FCSTD DOCUMENT  (FreeCAD 1.0R39109 (Git))
Label: lightModule
License: All rights reserved
LicenseURL: http://en.wikipedia.org/wiki/All_rights_reserved
objects: Part::Feature×41, Part::MultiFuse×37, Part::FeaturePython×27, Part::Extrusion×24, Sketcher::SketchObject×23, Part::Cylinder×20, Part::Cut×13, Part::Fillet×7, Part::Sphere×6, App::Part×5, Part::Compound×3, Part::Box×1, Part::Part2DObjectPython×1
note: 226 computed .brp shape members not serialized (recipe doc carries the construction recipe); baked Part::Feature solids carry a one-line shape summary decoded from their .brp

FEATURE [Part::Feature] Part__Feature330  label="elpCamera"
  Placement = pos=(0,-270,13) rot=(0,0,1;0rad)
  shape: bbox 38 x 38 x 25.12 mm, 164 faces (baked)
FEATURE [Part::Box] Box004  label="guva"
  AttacherType = Attacher::AttachEngine3D
  Height = 2
  Length = 19
  Placement = pos=(-9.5,-88,0) rot=(0,0,1;0rad)
  Width = 10
FEATURE [Part::Cylinder] Cylinder098
  Angle = 360
  AttacherType = Attacher::AttachEngine3D
  FirstAngle = 0
  Height = 10
  Placement = pos=(6.5,-83,0) rot=(0,0,1;0rad)
  Radius = 1.13
  SecondAngle = 0
FEATURE [Part::Cut] Cut018  label="guva001"
  Base = -> Box004
  Placement = pos=(80,-176.25,28) rot=(0,0,1;0rad)
  Tool = -> Cylinder098
FEATURE [Part::Feature] Part__Feature105  label="Printed Circuit Board"
  shape: bbox 25.4 x 17.78 x 1.6 mm, 42 faces (baked)
FEATURE [Part::Feature] Part__Feature106  label="EAHC2835WD6"
  shape: bbox 3.513 x 2.813 x 0.7485 mm, 108 faces, 4 solids (baked)
FEATURE [Part::Feature] Part__Feature107  label="AS7341 v2"
  Placement = pos=(0,-0.339822,1.6) rot=(0,0,1;0rad)
  shape: bbox 2 x 3.1 x 1.1 mm, 267 faces, 26 solids (baked)
FEATURE [Part::Feature] Part__Feature108  label="CAPC-0805-T0.95-BN v1"
  Placement = pos=(-5.01759,-3.15294,1.6) rot=(0,0,1;0rad)
  shape: bbox 2.1 x 1.35 x 0.95 mm, 42 faces (baked)
FEATURE [Part::Feature] Part__Feature109  label="CAPC-0805-T0.95-BN v002"
  Placement = pos=(-5.48627,2.66154,1.6) rot=(0,0,-1;1.5708rad)
  shape: bbox 1.35 x 2.1 x 0.95 mm, 42 faces (baked)
FEATURE [Part::Feature] Part__Feature110  label="CAPC-0805-T0.95-BN v003"
  Placement = pos=(-3.43627,2.66154,1.6) rot=(0,0,-1;1.5708rad)
  shape: bbox 1.35 x 2.1 x 0.95 mm, 42 faces (baked)
FEATURE [Part::Feature] Part__Feature111  label="CAPC-0603-T0.9-BN v1"
  Placement = pos=(-1.69987,-3.28475,1.6) rot=(0,0,1;0rad)
  shape: bbox 1.7 x 0.9 x 0.9 mm, 42 faces (baked)
FEATURE [Part::Feature] Part__Feature112  label="BODY_MF06A"
  Placement = pos=(0,0,0.762) rot=(0.57735,-0.57735,-0.57735;2.0944rad)
  shape: bbox 1.601 x 2.921 x 1.016 mm, 42 faces (baked)
FEATURE [Part::Feature] Part__Feature113  label="LEAD_MF06A"
  Placement = pos=(-0.9652,-0.9525,0.1016) rot=(0.57735,-0.57735,-0.57735;2.0944rad)
  shape: bbox 0.6223 x 0.3749 x 0.8636 mm, 14 faces (baked)
FEATURE [Part::Feature] Part__Feature114  label="LEAD_MF06A001"
  Placement = pos=(-0.9652,0,0.1016) rot=(0.57735,-0.57735,-0.57735;2.0944rad)
  shape: bbox 0.6223 x 0.3749 x 0.8636 mm, 14 faces (baked)
FEATURE [Part::Feature] Part__Feature115  label="LEAD_MF06A002"
  Placement = pos=(-0.9652,0.9525,0.1016) rot=(0.57735,-0.57735,-0.57735;2.0944rad)
  shape: bbox 0.6223 x 0.3749 x 0.8636 mm, 14 faces (baked)
FEATURE [Part::Feature] Part__Feature116  label="LEAD_MF06A003"
  Placement = pos=(0.9652,-0.9525,0.1016) rot=(0.57735,0.57735,0.57735;2.0944rad)
  shape: bbox 0.6223 x 0.3749 x 0.8636 mm, 14 faces (baked)
FEATURE [Part::Feature] Part__Feature117  label="LEAD_MF06A004"
  Placement = pos=(0.9652,0,0.1016) rot=(0.57735,0.57735,0.57735;2.0944rad)
  shape: bbox 0.6223 x 0.3749 x 0.8636 mm, 14 faces (baked)
FEATURE [Part::Feature] Part__Feature118  label="LEAD_MF06A005"
  Placement = pos=(0.9652,0.9525,0.1016) rot=(0.57735,0.57735,0.57735;2.0944rad)
  shape: bbox 0.6223 x 0.3749 x 0.8636 mm, 14 faces (baked)
FEATURE [Part::Feature] Part__Feature119  label="SOT363 v2"
  Placement = pos=(4.97054,-0.645171,1.675) rot=(0,0,1;3.14159rad)
  shape: bbox 2.1 x 2 x 1.1 mm, 94 faces, 7 solids (baked)
FEATURE [Part::Feature] Part__Feature120  label="LED 0603 single color v1"
  Placement = pos=(-9.18406,3.72778,1.60762) rot=(0,0,1;1.5708rad)
  shape: bbox 1.961 x 0.7932 x 0.7145 mm, 63 faces, 5 solids (baked)
FEATURE [Part::Feature] Part__Feature121  label="RESC-0603 v1"
  Placement = pos=(4.83432,-3.67461,1.6) rot=(0,0,1;0rad)
  shape: bbox 1.7 x 0.9 x 0.55 mm, 52 faces, 3 solids (baked)
FEATURE [Part::Feature] Part__Feature122  label="RESC-0603 v002"
  Placement = pos=(-7.14949,3.61248,1.6) rot=(0,0,-1;1.5708rad)
  shape: bbox 0.9 x 1.7 x 0.55 mm, 52 faces, 3 solids (baked)
FEATURE [Part::Feature] Part__Feature123  label="YC164_RESPACK v1"
  Placement = pos=(2.99591,1.52916,1.6) rot=(0,0,1;0rad)
  shape: bbox 3.2 x 1.6 x 0.61 mm, 172 faces (baked)
FEATURE [Part::Feature] Part__Feature124  label="qwicc v2"
  Placement = pos=(-10.8364,0.0607456,1.65) rot=(0,0,-1;1.5708rad)
  shape: bbox 4.95 x 6 x 2.96 mm, 229 faces, 7 solids (baked)
FEATURE [Part::Feature] Part__Feature125  label="qwicc v003"
  Placement = pos=(10.8256,0.00556102,1.65) rot=(0,0,1;1.5708rad)
  shape: bbox 4.95 x 6 x 2.96 mm, 229 faces, 7 solids (baked)
FEATURE [App::Part] sot_23_6_v2  label="sot-23-6 v2"
  Group = -> [Part__Feature112,Part__Feature113,Part__Feature114,Part__Feature115,Part__Feature116,Part__Feature117,Part__Feature118]
  Origin = -> Origin008
  Placement = pos=(-4.47945,-0.603742,1.69152) rot=(0,0,1;0rad)
FEATURE [App::Part] Adafruit_AS7341_STEMMA_QT_v2  label="ltr390"
  Group = -> [Part__Feature105,Part__Feature106,Part__Feature107,Part__Feature108,Part__Feature109,Part__Feature110,Part__Feature111,sot_23_6_v2,Part__Feature119,Part__Feature120,Part__Feature121,Part__Feature122,Part__Feature123,Part__Feature124,Part__Feature125]
  Origin = -> Origin009
  Placement = pos=(80,-274.25,28) rot=(0,0,1;0rad)
FEATURE [Part::FeaturePython] Clone  label="tSlotTop"  # WARN: FeaturePython — macro-defined, semantics opaque (R4)
  AttacherType = Attacher::AttachEngine3D
  Fuse = false
  Placement = pos=(0,0,-7) rot=(1,0,0;1.5708rad)
  Scale = (1,1,3)
FEATURE [Part::Sphere] Sphere011  label="Sphere_out005"
  Angle1 = -90
  Angle2 = 90
  Angle3 = 180
  AttacherType = Attacher::AttachEngine3D
  Placement = pos=(0,0,0) rot=(1,0,0;1.5708rad)
  Radius = 30
FEATURE [Part::Sphere] Sphere012  label="Sphere_in005"
  Angle1 = -90
  Angle2 = 90
  Angle3 = 180
  AttacherType = Attacher::AttachEngine3D
  Placement = pos=(0,0,0) rot=(1,0,0;1.5708rad)
  Radius = 28.7
FEATURE [Part::Cut] Cut065  label="Dome005"
  Base = -> Sphere011
  Tool = -> Sphere012
FEATURE [Part::Cylinder] Cylinder139
  Angle = 360
  AttacherType = Attacher::AttachEngine3D
  FirstAngle = 0
  Height = 2.6
  Radius = 40
  SecondAngle = 0
FEATURE [Part::Cylinder] Cylinder140  label="Cylinder_in005"
  Angle = 360
  AttacherType = Attacher::AttachEngine3D
  FirstAngle = 0
  Height = 2.6
  Radius = 30
  SecondAngle = 0
FEATURE [Part::Cut] Cut066  label="Base_flat005"
  Base = -> Cylinder139
  Tool = -> Cylinder140
FEATURE [Part::MultiFuse] Fusion  label="dome"
  Shapes = -> [Cut065,Cut066]
FEATURE [Sketcher::SketchObject] Sketch194
  ArcFitTolerance = 0
  FullyConstrained = true
  MakeInternals = false
  sketch-geometry (4):
    g0: Circle CenterX=0 CenterY=35 CenterZ=0 NormalX=0 NormalY=0 NormalZ=1 AngleXU=0 Radius=1.625
    g1: Circle CenterX=35 CenterY=0 CenterZ=0 NormalX=0 NormalY=0 NormalZ=1 AngleXU=0 Radius=1.625
    g2: Circle CenterX=-35 CenterY=0 CenterZ=0 NormalX=0 NormalY=0 NormalZ=1 AngleXU=0 Radius=1.625
    g3: Circle CenterX=0 CenterY=-35 CenterZ=0 NormalX=0 NormalY=0 NormalZ=1 AngleXU=0 Radius=1.625
  constraints (12):
    c: PointOnObject(g0,g-2)
    c: PointOnObject(g1,g-1)
    c: PointOnObject(g2,g-1)
    c: PointOnObject(g3,g-2)
    c: DistanceY(g3,g-1) = 35
    c: DistanceX(g-1,g1) = 35
    c: DistanceX(g2,g-1) = 35
    c: DistanceY(g-1,g0) = 35
    c: Equal(g1,g3)
    c: Equal(g1,g2)
    c: Equal(g1,g0)
    c: Diameter(g1) = 3.25
FEATURE [Part::Extrusion] Extrude091
  Base = -> Sketch194
  Dir = (0,0,1)
  DirMode = 2
  FaceMakerClass = Part::FaceMakerBullseye
  FaceMakerMode = 3
  LengthFwd = 10
  LengthRev = 0
  Solid = true
  Symmetric = false
FEATURE [Part::Cut] Cut067  label="dome001"
  Base = -> Fusion
  Placement = pos=(0,-270,30.5) rot=(0,0,1;0rad)
  Tool = -> Extrude091
FEATURE [Part::Cylinder] Cylinder141
  Angle = 360
  AttacherType = Attacher::AttachEngine3D
  FirstAngle = 0
  Height = 2.6
  Radius = 40
  SecondAngle = 0
FEATURE [Part::Cylinder] Cylinder142  label="Cylinder_in006"
  Angle = 360
  AttacherType = Attacher::AttachEngine3D
  FirstAngle = 0
  Height = 2.6
  Radius = 30
  SecondAngle = 0
FEATURE [Part::Cut] Cut069  label="Base_flat006"
  Base = -> Cylinder141
  Tool = -> Cylinder142
FEATURE [Sketcher::SketchObject] Sketch195
  ArcFitTolerance = 0
  FullyConstrained = true
  MakeInternals = false
  sketch-geometry (4):
    g0: Circle CenterX=0 CenterY=35 CenterZ=0 NormalX=0 NormalY=0 NormalZ=1 AngleXU=0 Radius=1.625
    g1: Circle CenterX=35 CenterY=0 CenterZ=0 NormalX=0 NormalY=0 NormalZ=1 AngleXU=0 Radius=1.625
    g2: Circle CenterX=-35 CenterY=0 CenterZ=0 NormalX=0 NormalY=0 NormalZ=1 AngleXU=0 Radius=1.625
    g3: Circle CenterX=0 CenterY=-35 CenterZ=0 NormalX=0 NormalY=0 NormalZ=1 AngleXU=0 Radius=1.625
  constraints (12):
    c: PointOnObject(g0,g-2)
    c: PointOnObject(g1,g-1)
    c: PointOnObject(g2,g-1)
    c: PointOnObject(g3,g-2)
    c: DistanceY(g3,g-1) = 35
    c: DistanceX(g-1,g1) = 35
    c: DistanceX(g2,g-1) = 35
    c: DistanceY(g-1,g0) = 35
    c: Equal(g1,g3)
    c: Equal(g1,g2)
    c: Equal(g1,g0)
    c: Diameter(g1) = 3.25
FEATURE [Part::Extrusion] Extrude092
  Base = -> Sketch195
  Dir = (0,0,1)
  DirMode = 2
  FaceMakerClass = Part::FaceMakerBullseye
  FaceMakerMode = 3
  LengthFwd = 10
  LengthRev = 0
  Solid = true
  Symmetric = false
FEATURE [Part::Sphere] Sphere013  label="Sphere_out006"
  Angle1 = -90
  Angle2 = 90
  Angle3 = 180
  AttacherType = Attacher::AttachEngine3D
  Placement = pos=(0,0,0) rot=(1,0,0;1.5708rad)
  Radius = 30
FEATURE [Part::Sphere] Sphere014  label="Sphere_in006"
  Angle1 = -90
  Angle2 = 90
  Angle3 = 180
  AttacherType = Attacher::AttachEngine3D
  Placement = pos=(0,0,0) rot=(1,0,0;1.5708rad)
  Radius = 28.7
FEATURE [Part::Cut] Cut068  label="Dome006"
  Base = -> Sphere013
  Tool = -> Sphere014
FEATURE [Part::MultiFuse] Fusion187  label="dome003"
  Shapes = -> [Cut068,Cut069]
FEATURE [Part::Cut] Cut070  label="dome002"
  Base = -> Fusion187
  Placement = pos=(-80,-270,30.5) rot=(0,0,1;0rad)
  Tool = -> Extrude092
FEATURE [Part::Cylinder] Cylinder143
  Angle = 360
  AttacherType = Attacher::AttachEngine3D
  FirstAngle = 0
  Height = 2.6
  Radius = 40
  SecondAngle = 0
FEATURE [Part::Cylinder] Cylinder144  label="Cylinder_in007"
  Angle = 360
  AttacherType = Attacher::AttachEngine3D
  FirstAngle = 0
  Height = 2.6
  Radius = 30
  SecondAngle = 0
FEATURE [Part::Cut] Cut072  label="Base_flat007"
  Base = -> Cylinder143
  Tool = -> Cylinder144
FEATURE [Sketcher::SketchObject] Sketch196
  ArcFitTolerance = 0
  FullyConstrained = true
  MakeInternals = false
  sketch-geometry (4):
    g0: Circle CenterX=0 CenterY=35 CenterZ=0 NormalX=0 NormalY=0 NormalZ=1 AngleXU=0 Radius=1.625
    g1: Circle CenterX=35 CenterY=0 CenterZ=0 NormalX=0 NormalY=0 NormalZ=1 AngleXU=0 Radius=1.625
    g2: Circle CenterX=-35 CenterY=0 CenterZ=0 NormalX=0 NormalY=0 NormalZ=1 AngleXU=0 Radius=1.625
    g3: Circle CenterX=0 CenterY=-35 CenterZ=0 NormalX=0 NormalY=0 NormalZ=1 AngleXU=0 Radius=1.625
  constraints (12):
    c: PointOnObject(g0,g-2)
    c: PointOnObject(g1,g-1)
    c: PointOnObject(g2,g-1)
    c: PointOnObject(g3,g-2)
    c: DistanceY(g3,g-1) = 35
    c: DistanceX(g-1,g1) = 35
    c: DistanceX(g2,g-1) = 35
    c: DistanceY(g-1,g0) = 35
    c: Equal(g1,g3)
    c: Equal(g1,g2)
    c: Equal(g1,g0)
    c: Diameter(g1) = 3.25
FEATURE [Part::Extrusion] Extrude093
  Base = -> Sketch196
  Dir = (0,0,1)
  DirMode = 2
  FaceMakerClass = Part::FaceMakerBullseye
  FaceMakerMode = 3
  LengthFwd = 10
  LengthRev = 0
  Solid = true
  Symmetric = false
FEATURE [Part::Sphere] Sphere015  label="Sphere_out007"
  Angle1 = -90
  Angle2 = 90
  Angle3 = 180
  AttacherType = Attacher::AttachEngine3D
  Placement = pos=(0,0,0) rot=(1,0,0;1.5708rad)
  Radius = 30
FEATURE [Part::Sphere] Sphere016  label="Sphere_in007"
  Angle1 = -90
  Angle2 = 90
  Angle3 = 180
  AttacherType = Attacher::AttachEngine3D
  Placement = pos=(0,0,0) rot=(1,0,0;1.5708rad)
  Radius = 28.7
FEATURE [Part::Cut] Cut071  label="Dome007"
  Base = -> Sphere015
  Tool = -> Sphere016
FEATURE [Part::MultiFuse] Fusion188  label="dome005"
  Shapes = -> [Cut071,Cut072]
FEATURE [Part::Cut] Cut073  label="dome004"
  Base = -> Fusion188
  Placement = pos=(80,-270,30.5) rot=(0,0,1;0rad)
  Tool = -> Extrude093
FEATURE [Sketcher::SketchObject] Sketch
  ArcFitTolerance = 0
  FullyConstrained = true
  MakeInternals = false
  Placement = pos=(0,0,27.5) rot=(0,0,1;0rad)
  sketch-geometry (2):
    g0: Circle CenterX=0 CenterY=-270 CenterZ=0 NormalX=0 NormalY=0 NormalZ=1 AngleXU=0 Radius=37
    g1: Circle CenterX=0 CenterY=-270 CenterZ=0 NormalX=0 NormalY=0 NormalZ=1 AngleXU=0 Radius=26.5
  constraints (5):
    c: Diameter(g0) = 74
    c: Coincident(g1,g0)
    c: Diameter(g1) = 53
    c: DistanceX(g0) = 0
    c: DistanceY(g0) = -270
FEATURE [Part::Extrusion] Extrude094  label="rubberSeals"
  Base = -> Sketch
  Dir = (0,0,1)
  DirMode = 2
  FaceMakerClass = Part::FaceMakerBullseye
  FaceMakerMode = 3
  LengthFwd = 3
  LengthRev = 0
  Solid = true
  Symmetric = false
FEATURE [Sketcher::SketchObject] Sketch197
  ArcFitTolerance = 0
  FullyConstrained = true
  MakeInternals = false
  Placement = pos=(0,0,27.5) rot=(0,0,1;0rad)
  sketch-geometry (2):
    g0: Circle CenterX=0 CenterY=-270 CenterZ=0 NormalX=0 NormalY=0 NormalZ=1 AngleXU=0 Radius=37
    g1: Circle CenterX=0 CenterY=-270 CenterZ=0 NormalX=0 NormalY=0 NormalZ=1 AngleXU=0 Radius=26.5
  constraints (5):
    c: Diameter(g0) = 74
    c: Coincident(g1,g0)
    c: Diameter(g1) = 53
    c: DistanceX(g0) = 0
    c: DistanceY(g0) = -270
FEATURE [Part::Extrusion] Extrude095  label="rubberSeals001"
  Base = -> Sketch197
  Dir = (0,0,1)
  DirMode = 2
  FaceMakerClass = Part::FaceMakerBullseye
  FaceMakerMode = 3
  LengthFwd = 3
  LengthRev = 0
  Placement = pos=(-80,0,0) rot=(0,0,1;0rad)
  Solid = true
  Symmetric = false
FEATURE [Sketcher::SketchObject] Sketch198
  ArcFitTolerance = 0
  FullyConstrained = true
  MakeInternals = false
  Placement = pos=(0,0,27.5) rot=(0,0,1;0rad)
  sketch-geometry (2):
    g0: Circle CenterX=0 CenterY=-270 CenterZ=0 NormalX=0 NormalY=0 NormalZ=1 AngleXU=0 Radius=37
    g1: Circle CenterX=0 CenterY=-270 CenterZ=0 NormalX=0 NormalY=0 NormalZ=1 AngleXU=0 Radius=26.5
  constraints (5):
    c: Diameter(g0) = 74
    c: Coincident(g1,g0)
    c: Diameter(g1) = 53
    c: DistanceX(g0) = 0
    c: DistanceY(g0) = -270
FEATURE [Part::Extrusion] Extrude096  label="rubberSeals002"
  Base = -> Sketch198
  Dir = (0,0,1)
  DirMode = 2
  FaceMakerClass = Part::FaceMakerBullseye
  FaceMakerMode = 3
  LengthFwd = 3
  LengthRev = 0
  Placement = pos=(80,0,0) rot=(0,0,1;0rad)
  Solid = true
  Symmetric = false
FEATURE [Part::Compound] Compound001  label="domesAndSeals"
  Links = -> [Cut067,Cut070,Cut073,Extrude094,Extrude095,Extrude096]
FEATURE [Sketcher::SketchObject] Sketch199
  ArcFitTolerance = 0
  FullyConstrained = true
  MakeInternals = false
  sketch-geometry (8):
    g0: LineSegment StartX=-98 StartY=-249.5 StartZ=0 EndX=-62 EndY=-249.5 EndZ=0
    g1: LineSegment StartX=-62 StartY=-249.5 StartZ=0 EndX=-62 EndY=-290.5 EndZ=0
    g2: LineSegment StartX=-62 StartY=-290.5 StartZ=0 EndX=-98 EndY=-290.5 EndZ=0
    g3: LineSegment StartX=-98 StartY=-290.5 StartZ=0 EndX=-98 EndY=-249.5 EndZ=0
    g4: Circle CenterX=-90 CenterY=-252.5 CenterZ=0 NormalX=0 NormalY=0 NormalZ=1 AngleXU=0 Radius=1.625
    g5: Circle CenterX=-70 CenterY=-252.5 CenterZ=0 NormalX=0 NormalY=0 NormalZ=1 AngleXU=0 Radius=1.625
    g6: Circle CenterX=-90 CenterY=-287.5 CenterZ=0 NormalX=0 NormalY=0 NormalZ=1 AngleXU=0 Radius=1.625
    g7: Circle CenterX=-70 CenterY=-287.5 CenterZ=0 NormalX=0 NormalY=0 NormalZ=1 AngleXU=0 Radius=1.625
  constraints (24):
    c: Coincident(g0,g1)
    c: Coincident(g1,g2)
    c: Coincident(g2,g3)
    c: Coincident(g3,g0)
    c: Horizontal(g0)
    c: Horizontal(g2)
    c: Vertical(g1)
    c: Vertical(g3)
    c: DistanceY(g2) = -290.5
    c: DistanceY(g2,g0) = 41
    c: Horizontal(g6,g7)
    c: Horizontal(g4,g5)
    c: Vertical(g4,g6)
    c: Vertical(g7,g5)
    c: DistanceY(g6) = -287.5
    c: DistanceY(g6,g4) = 35
    c: DistanceX(g6,g7) = 20
    c: Equal(g5,g7)
    c: Equal(g5,g6)
    c: Equal(g5,g4)
    c: Diameter(g5) = 3.25
    c: DistanceX(g2,g1) = 36
    c: DistanceX(g1) = -62
    c: DistanceX(g7,g1) = 8
FEATURE [Part::Extrusion] Extrude097  label="as7265x001"
  Base = -> Sketch199
  Dir = (0,0,1)
  DirMode = 2
  FaceMakerClass = Part::FaceMakerBullseye
  FaceMakerMode = 3
  LengthFwd = 2
  LengthRev = 0
  Placement = pos=(0,0,28) rot=(0,0,1;0rad)
  Solid = true
  Symmetric = false
FEATURE [Part::Feature] Part__Feature  label="Printed Circuit Board001"
  shape: bbox 25.4 x 20.32 x 1.65 mm, 39 faces (baked)
FEATURE [Part::Feature] Part__Feature331  label="RESC-2512-R100 v2"
  Placement = pos=(0.0152473,1.04463,1.65) rot=(0,0,1;3.14159rad)
  shape: bbox 6.417 x 3.317 x 0.6674 mm, 219 faces, 7 solids (baked)
FEATURE [Part::Feature] Part__Feature332  label="LED 0603 single color v002"
  Placement = pos=(-9.06678,4.19381,1.65762) rot=(0,0,1;1.5708rad)
  shape: bbox 1.961 x 0.7932 x 0.7145 mm, 63 faces, 5 solids (baked)
FEATURE [Part::Feature] Part__Feature333  label="CAPC-0805-T0.95-BN v004"
  Placement = pos=(-4.32049,-3.03839,1.65) rot=(0,0,-1;1.5708rad)
  shape: bbox 1.35 x 2.1 x 0.95 mm, 42 faces (baked)
FEATURE [Part::Feature] Part__Feature334  label="CAPC-0603-T0.9-BN v002"
  Placement = pos=(-2.53733,-2.97022,1.65) rot=(0,0,-1;1.5708rad)
  shape: bbox 0.9 x 1.7 x 0.9 mm, 42 faces (baked)
FEATURE [Part::Feature] Part__Feature335  label="RESC-0603 v003"
  Placement = pos=(-7.09227,3.55774,1.65) rot=(0,0,-1;1.5708rad)
  shape: bbox 0.9 x 1.7 x 0.55 mm, 52 faces, 3 solids (baked)
FEATURE [Part::Feature] Part__Feature336  label="YC164_RESPACK v002"
  Placement = pos=(2.74348,-1.41846,1.65) rot=(0,0,-1;1.5708rad)
  shape: bbox 1.6 x 3.2 x 0.61 mm, 172 faces (baked)
FEATURE [Part::Feature] Part__Feature337  label="qwicc v1"
  Placement = pos=(-8.57299,-0.000230516,1.345) rot=(0.57735,-0.57735,-0.57735;2.0944rad)
  shape: bbox 4.95 x 6 x 2.96 mm, 229 faces, 7 solids (baked)
FEATURE [Part::Feature] Part__Feature338  label="qwicc v004"
  Placement = pos=(8.61502,0.00281866,1.345) rot=(0.57735,0.57735,0.57735;2.0944rad)
  shape: bbox 4.95 x 6 x 2.96 mm, 229 faces, 7 solids (baked)
FEATURE [Part::Feature] Part__Feature339  label="B219 v2"
  Placement = pos=(0.00220704,-3.21564,1.62965) rot=(0,0,1;3.14159rad)
  shape: bbox 3.008 x 2.843 x 1.194 mm, 338 faces, 14 solids (baked)
FEATURE [Part::Feature] Part__Feature340  label="Screw Terminal 2pin 3.5mm Pitch v11"
  Placement = pos=(0.115254,6.14583,1.45) rot=(0,0,1;3.14159rad)
  shape: bbox 11.43 x 7.244 x 12 mm, 100 faces, 3 solids (baked)
FEATURE [App::Part] Adafruit_INA219_STEMMA_QT_v7  label="ina219"
  Group = -> [Part__Feature,Part__Feature331,Part__Feature332,Part__Feature333,Part__Feature334,Part__Feature335,Part__Feature336,Part__Feature337,Part__Feature338,Part__Feature339,Part__Feature340]
  Origin = -> Origin
  Placement = pos=(58,-270,9) rot=(0,-1,0;4.71239rad)
FEATURE [Part::Feature] Part__Feature343  label="Body"
  shape: bbox 15.5 x 16.75 x 29 mm, 21 faces (baked)
FEATURE [Part::Feature] Part__Feature344  label="Body001"
  Placement = pos=(0,0,2) rot=(0,0,1;0rad)
  shape: bbox 17.44 x 17.44 x 14.25 mm, 14 faces (baked)
FEATURE [Part::Feature] Part__Feature345  label="Body002"
  Placement = pos=(0,0,-2.9) rot=(0,0,1;0rad)
  shape: bbox 19 x 19 x 4.75 mm, 25 faces (baked)
FEATURE [Part::Feature] Part__Feature346  label="Body003"
  shape: bbox 16.75 x 16.75 x 0.9 mm, 4 faces (baked)
FEATURE [App::Part] PG7_Gland1
  Group = -> [Part__Feature343,Part__Feature344,Part__Feature345,Part__Feature346]
  Origin = -> Origin010
  Placement = pos=(72,-256,-26) rot=(0,-1,0;3.14159rad)
FEATURE [Part::Feature] Part__Feature347  label="Body004"
  shape: bbox 15.5 x 16.75 x 29 mm, 21 faces (baked)
FEATURE [Part::Feature] Part__Feature348  label="Body005"
  Placement = pos=(0,0,2) rot=(0,0,1;0rad)
  shape: bbox 17.44 x 17.44 x 14.25 mm, 14 faces (baked)
FEATURE [Part::Feature] Part__Feature349  label="Body006"
  Placement = pos=(0,0,-2.9) rot=(0,0,1;0rad)
  shape: bbox 19 x 19 x 4.75 mm, 25 faces (baked)
FEATURE [Part::Feature] Part__Feature350  label="Body007"
  shape: bbox 16.75 x 16.75 x 0.9 mm, 4 faces (baked)
FEATURE [App::Part] PG7_Gland002
  Group = -> [Part__Feature347,Part__Feature348,Part__Feature349,Part__Feature350]
  Origin = -> Origin011
  Placement = pos=(0,-256,-26) rot=(0,-1,0;3.14159rad)
FEATURE [Part::FeaturePython] Clone027  label="M3Nut050"  # WARN: FeaturePython — macro-defined, semantics opaque (R4)
  AttacherType = Attacher::AttachEngine3D
  Fuse = false
  Placement = pos=(0,0,4.5) rot=(0,0,1;0rad)
  Scale = (1.1,1.1,5)
FEATURE [Part::FeaturePython] Clone028  label="M3Nut051"  # WARN: FeaturePython — macro-defined, semantics opaque (R4)
  AttacherType = Attacher::AttachEngine3D
  Fuse = false
  Placement = pos=(0,0,0.9) rot=(0,0,1;0rad)
  Scale = (1.1,1.1,1)
FEATURE [Part::FeaturePython] Clone029  label="M3Nut052"  # WARN: FeaturePython — macro-defined, semantics opaque (R4)
  AttacherType = Attacher::AttachEngine3D
  Fuse = false
  Placement = pos=(0,0,4.5) rot=(0,0,1;0rad)
  Scale = (1.1,1.1,5)
FEATURE [Part::FeaturePython] Clone030  label="M3Nut053"  # WARN: FeaturePython — macro-defined, semantics opaque (R4)
  AttacherType = Attacher::AttachEngine3D
  Fuse = false
  Placement = pos=(0,0,0.9) rot=(0,0,1;0rad)
  Scale = (1.1,1.1,1)
FEATURE [Part::FeaturePython] Clone031  label="M3Nut054"  # WARN: FeaturePython — macro-defined, semantics opaque (R4)
  AttacherType = Attacher::AttachEngine3D
  Fuse = false
  Placement = pos=(0,0,4.5) rot=(0,0,1;0rad)
  Scale = (1.1,1.1,5)
FEATURE [Part::FeaturePython] Clone032  label="M3Nut055"  # WARN: FeaturePython — macro-defined, semantics opaque (R4)
  AttacherType = Attacher::AttachEngine3D
  Fuse = false
  Placement = pos=(0,0,0.9) rot=(0,0,1;0rad)
  Scale = (1.1,1.1,1)
FEATURE [Part::FeaturePython] Clone033  label="M3Nut056"  # WARN: FeaturePython — macro-defined, semantics opaque (R4)
  AttacherType = Attacher::AttachEngine3D
  Fuse = false
  Placement = pos=(0,0,4.5) rot=(0,0,1;0rad)
  Scale = (1.1,1.1,5)
FEATURE [Part::FeaturePython] Clone034  label="M3Nut057"  # WARN: FeaturePython — macro-defined, semantics opaque (R4)
  AttacherType = Attacher::AttachEngine3D
  Fuse = false
  Placement = pos=(0,0,0.9) rot=(0,0,1;0rad)
  Scale = (1.1,1.1,1)
FEATURE [Part::FeaturePython] Clone035  label="M3Nut058"  # WARN: FeaturePython — macro-defined, semantics opaque (R4)
  AttacherType = Attacher::AttachEngine3D
  Fuse = false
  Placement = pos=(0,0,4.5) rot=(0,0,1;0rad)
  Scale = (1.1,1.1,5)
FEATURE [Part::FeaturePython] Clone036  label="M3Nut059"  # WARN: FeaturePython — macro-defined, semantics opaque (R4)
  AttacherType = Attacher::AttachEngine3D
  Fuse = false
  Placement = pos=(0,0,0.9) rot=(0,0,1;0rad)
  Scale = (1.1,1.1,1)
FEATURE [Part::FeaturePython] Clone037  label="M3Nut060"  # WARN: FeaturePython — macro-defined, semantics opaque (R4)
  AttacherType = Attacher::AttachEngine3D
  Fuse = false
  Placement = pos=(0,0,4.5) rot=(0,0,1;0rad)
  Scale = (1.1,1.1,5)
FEATURE [Part::FeaturePython] Clone038  label="M3Nut061"  # WARN: FeaturePython — macro-defined, semantics opaque (R4)
  AttacherType = Attacher::AttachEngine3D
  Fuse = false
  Placement = pos=(0,0,0.9) rot=(0,0,1;0rad)
  Scale = (1.1,1.1,1)
FEATURE [Part::FeaturePython] Clone039  label="M3Nut062"  # WARN: FeaturePython — macro-defined, semantics opaque (R4)
  AttacherType = Attacher::AttachEngine3D
  Fuse = false
  Placement = pos=(0,0,4.5) rot=(0,0,1;0rad)
  Scale = (1.1,1.1,5)
FEATURE [Part::FeaturePython] Clone040  label="M3Nut063"  # WARN: FeaturePython — macro-defined, semantics opaque (R4)
  AttacherType = Attacher::AttachEngine3D
  Fuse = false
  Placement = pos=(0,0,0.9) rot=(0,0,1;0rad)
  Scale = (1.1,1.1,1)
FEATURE [Part::FeaturePython] Clone041  label="M3Nut064"  # WARN: FeaturePython — macro-defined, semantics opaque (R4)
  AttacherType = Attacher::AttachEngine3D
  Fuse = false
  Placement = pos=(0,0,4.5) rot=(0,0,1;0rad)
  Scale = (1.1,1.1,5)
FEATURE [Part::FeaturePython] Clone042  label="M3Nut065"  # WARN: FeaturePython — macro-defined, semantics opaque (R4)
  AttacherType = Attacher::AttachEngine3D
  Fuse = false
  Placement = pos=(0,0,0.9) rot=(0,0,1;0rad)
  Scale = (1.1,1.1,1)
FEATURE [Part::FeaturePython] Clone043  label="M3Nut066"  # WARN: FeaturePython — macro-defined, semantics opaque (R4)
  AttacherType = Attacher::AttachEngine3D
  Fuse = false
  Placement = pos=(0,0,4.5) rot=(0,0,1;0rad)
  Scale = (1.1,1.1,5)
FEATURE [Part::FeaturePython] Clone044  label="M3Nut067"  # WARN: FeaturePython — macro-defined, semantics opaque (R4)
  AttacherType = Attacher::AttachEngine3D
  Fuse = false
  Placement = pos=(0,0,0.9) rot=(0,0,1;0rad)
  Scale = (1.1,1.1,1)
FEATURE [Part::FeaturePython] Clone045  label="M3Nut068"  # WARN: FeaturePython — macro-defined, semantics opaque (R4)
  AttacherType = Attacher::AttachEngine3D
  Fuse = false
  Placement = pos=(0,0,4.5) rot=(0,0,1;0rad)
  Scale = (1.1,1.1,5)
FEATURE [Part::FeaturePython] Clone046  label="M3Nut069"  # WARN: FeaturePython — macro-defined, semantics opaque (R4)
  AttacherType = Attacher::AttachEngine3D
  Fuse = false
  Placement = pos=(0,0,0.9) rot=(0,0,1;0rad)
  Scale = (1.1,1.1,1)
FEATURE [Part::FeaturePython] Clone047  label="M3Nut070"  # WARN: FeaturePython — macro-defined, semantics opaque (R4)
  AttacherType = Attacher::AttachEngine3D
  Fuse = false
  Placement = pos=(0,0,4.5) rot=(0,0,1;0rad)
  Scale = (1.1,1.1,5)
FEATURE [Part::FeaturePython] Clone048  label="M3Nut071"  # WARN: FeaturePython — macro-defined, semantics opaque (R4)
  AttacherType = Attacher::AttachEngine3D
  Fuse = false
  Placement = pos=(0,0,0.9) rot=(0,0,1;0rad)
  Scale = (1.1,1.1,1)
FEATURE [Part::FeaturePython] Clone049  label="M3Nut072"  # WARN: FeaturePython — macro-defined, semantics opaque (R4)
  AttacherType = Attacher::AttachEngine3D
  Fuse = false
  Placement = pos=(0,0,4.5) rot=(0,0,1;0rad)
  Scale = (1.1,1.1,5)
FEATURE [Part::FeaturePython] Clone050  label="M3Nut073"  # WARN: FeaturePython — macro-defined, semantics opaque (R4)
  AttacherType = Attacher::AttachEngine3D
  Fuse = false
  Placement = pos=(0,0,0.9) rot=(0,0,1;0rad)
  Scale = (1.1,1.1,1)
FEATURE [Part::FeaturePython] Clone051  label="M3Nut074"  # WARN: FeaturePython — macro-defined, semantics opaque (R4)
  AttacherType = Attacher::AttachEngine3D
  Fuse = false
  Placement = pos=(0,0,4.5) rot=(0,0,1;0rad)
  Scale = (1.1,1.1,5)
FEATURE [Part::FeaturePython] Clone052  label="M3Nut075"  # WARN: FeaturePython — macro-defined, semantics opaque (R4)
  AttacherType = Attacher::AttachEngine3D
  Fuse = false
  Placement = pos=(0,0,0.9) rot=(0,0,1;0rad)
  Scale = (1.1,1.1,1)
FEATURE [Part::Cylinder] Cylinder157 .. Cylinder169  x13 (patterned run collapsed; names and placements below)
  Angle = 360
  AttacherType = Attacher::AttachEngine3D
  FirstAngle = 0
  Height = 9
  Radius = 2
  SecondAngle = 0
FEATURE [Part::MultiFuse] Fusion223
  Shapes = -> [Clone027,Cylinder157]
FEATURE [Part::MultiFuse] Fusion224  label="m3NutCut014"
  Placement = pos=(-80,-235,-22.5) rot=(0.707107,-0.707107,0;3.14159rad)
  Shapes = -> [Clone028,Fusion223]
FEATURE [Part::MultiFuse] Fusion227
  Shapes = -> [Clone029,Cylinder158]
FEATURE [Part::MultiFuse] Fusion228  label="m3NutCut015"
  Placement = pos=(-115,-270,-22.5) rot=(1,0,0;3.14159rad)
  Shapes = -> [Clone030,Fusion227]
FEATURE [Part::MultiFuse] Fusion229
  Shapes = -> [Clone031,Cylinder159]
FEATURE [Part::MultiFuse] Fusion230  label="m3NutCut016"
  Placement = pos=(-45,-270,-22.5) rot=(1,0,0;3.14159rad)
  Shapes = -> [Clone032,Fusion229]
FEATURE [Part::MultiFuse] Fusion231
  Shapes = -> [Clone033,Cylinder160]
FEATURE [Part::MultiFuse] Fusion232  label="m3NutCut017"
  Placement = pos=(-35,-270,-22.5) rot=(1,0,0;3.14159rad)
  Shapes = -> [Clone034,Fusion231]
FEATURE [Part::MultiFuse] Fusion233
  Shapes = -> [Clone035,Cylinder161]
FEATURE [Part::MultiFuse] Fusion234  label="m3NutCut018"
  Placement = pos=(35,-270,-22.5) rot=(1,0,0;3.14159rad)
  Shapes = -> [Clone036,Fusion233]
FEATURE [Part::MultiFuse] Fusion235
  Shapes = -> [Clone037,Cylinder162]
FEATURE [Part::MultiFuse] Fusion236  label="m3NutCut019"
  Placement = pos=(45,-270,-22.5) rot=(1,0,0;3.14159rad)
  Shapes = -> [Clone038,Fusion235]
FEATURE [Part::MultiFuse] Fusion237
  Shapes = -> [Clone039,Cylinder163]
FEATURE [Part::MultiFuse] Fusion238  label="m3NutCut020"
  Placement = pos=(115,-270,-22.5) rot=(1,0,0;3.14159rad)
  Shapes = -> [Clone040,Fusion237]
FEATURE [Part::MultiFuse] Fusion239
  Shapes = -> [Clone041,Cylinder164]
FEATURE [Part::MultiFuse] Fusion240  label="m3NutCut021"
  Placement = pos=(-80,-235,-22.5) rot=(0.707107,-0.707107,0;3.14159rad)
  Shapes = -> [Clone042,Fusion239]
FEATURE [Part::MultiFuse] Fusion241
  Shapes = -> [Clone043,Cylinder165]
FEATURE [Part::MultiFuse] Fusion242  label="m3NutCut022"
  Placement = pos=(0,-235,-22.5) rot=(0.707107,-0.707107,0;3.14159rad)
  Shapes = -> [Clone044,Fusion241]
FEATURE [Part::MultiFuse] Fusion243
  Shapes = -> [Clone045,Cylinder166]
FEATURE [Part::MultiFuse] Fusion244  label="m3NutCut023"
  Placement = pos=(80,-235,-22.5) rot=(0.707107,-0.707107,0;3.14159rad)
  Shapes = -> [Clone046,Fusion243]
FEATURE [Part::MultiFuse] Fusion245
  Shapes = -> [Clone047,Cylinder167]
FEATURE [Part::MultiFuse] Fusion246  label="m3NutCut024"
  Placement = pos=(80,-305,-22.5) rot=(0.707107,-0.707107,0;3.14159rad)
  Shapes = -> [Clone048,Fusion245]
FEATURE [Part::MultiFuse] Fusion247
  Shapes = -> [Clone049,Cylinder168]
FEATURE [Part::MultiFuse] Fusion248  label="m3NutCut025"
  Placement = pos=(1.4e-14,-305,-22.5) rot=(0.707107,-0.707107,0;3.14159rad)
  Shapes = -> [Clone050,Fusion247]
FEATURE [Part::MultiFuse] Fusion249
  Shapes = -> [Clone051,Cylinder169]
FEATURE [Part::MultiFuse] Fusion250  label="m3NutCut026"
  Placement = pos=(-80,-305,-22.5) rot=(0.707107,-0.707107,0;3.14159rad)
  Shapes = -> [Clone052,Fusion249]
FEATURE [Part::MultiFuse] Fusion251  label="m3NutCuts"
  Placement = pos=(0,0,-0.5) rot=(0,0,1;0rad)
  Shapes = -> [Fusion224,Fusion228,Fusion230,Fusion232,Fusion234,Fusion236,Fusion238,Fusion240,Fusion242,Fusion244,Fusion246,Fusion248,Fusion250]
FEATURE [Part::Part2DObjectPython] ShapeString001  # Draft 2D object (typed FeaturePython)
  FontFile = <userpath>/gitHubRepos/3DMints2024/msclns/fonts/montserrat/Montserrat-Regular.otf
  Fuse = false
  Justification = 6
  JustificationReference = 0
  KeepLeftMargin = false
  MakeFace = true
  ObliqueAngle = 0
  Placement = pos=(-15.5,-310,-21) rot=(1,0,0;1.5708rad)
  ScaleToSize = true
  Size = 15
  String = MINTS-AI
  Tracking = 0
FEATURE [Part::Extrusion] Extrude129  label="text"
  Base = -> ShapeString001
  Dir = (0,-1,2e-16)
  DirMode = 2
  FaceMakerClass = Part::FaceMakerBullseye
  FaceMakerMode = 3
  LengthFwd = 2
  LengthRev = 0
  Solid = false
  Symmetric = false
FEATURE [Sketcher::SketchObject] Sketch220
  ArcFitTolerance = 0
  FullyConstrained = true
  MakeInternals = false
  Placement = pos=(0,0,-25) rot=(0,0,1;0rad)
  sketch-geometry (12):
    g0: Circle CenterX=-115 CenterY=-270 CenterZ=0 NormalX=0 NormalY=0 NormalZ=1 AngleXU=0 Radius=1.625
    g1: Circle CenterX=-80 CenterY=-235 CenterZ=0 NormalX=0 NormalY=0 NormalZ=1 AngleXU=0 Radius=1.625
    g2: Circle CenterX=-80 CenterY=-305 CenterZ=0 NormalX=0 NormalY=0 NormalZ=1 AngleXU=0 Radius=1.625
    g3: Circle CenterX=-45 CenterY=-270 CenterZ=0 NormalX=0 NormalY=0 NormalZ=1 AngleXU=0 Radius=1.625
    g4: Circle CenterX=-35 CenterY=-270 CenterZ=0 NormalX=0 NormalY=0 NormalZ=1 AngleXU=0 Radius=1.625
    g5: Circle CenterX=0 CenterY=-305 CenterZ=0 NormalX=0 NormalY=0 NormalZ=1 AngleXU=0 Radius=1.625
    g6: Circle CenterX=0 CenterY=-235 CenterZ=0 NormalX=0 NormalY=0 NormalZ=1 AngleXU=0 Radius=1.625
    g7: Circle CenterX=35 CenterY=-270 CenterZ=0 NormalX=0 NormalY=0 NormalZ=1 AngleXU=0 Radius=1.625
    g8: Circle CenterX=45 CenterY=-270 CenterZ=0 NormalX=0 NormalY=0 NormalZ=1 AngleXU=0 Radius=1.625
    g9: Circle CenterX=80 CenterY=-235 CenterZ=0 NormalX=0 NormalY=0 NormalZ=1 AngleXU=0 Radius=1.625
    g10: Circle CenterX=115 CenterY=-270 CenterZ=0 NormalX=0 NormalY=0 NormalZ=1 AngleXU=0 Radius=1.625
    g11: Circle CenterX=80 CenterY=-305 CenterZ=0 NormalX=0 NormalY=0 NormalZ=1 AngleXU=0 Radius=1.625
  constraints (36):
    c: PointOnObject(g5,g-2)
    c: PointOnObject(g6,g-2)
    c: Equal(g8,g1)
    c: Equal(g8,g6)
    c: Equal(g8,g9)
    c: Equal(g8,g2)
    c: Equal(g8,g5)
    c: Equal(g8,g11)
    c: Equal(g8,g0)
    c: Equal(g8,g3)
    c: Equal(g8,g4)
    c: Equal(g8,g7)
    c: Equal(g8,g10)
    c: Diameter(g8) = 3.25
    c: Horizontal(g0,g3)
    c: Horizontal(g3,g4)
    c: Horizontal(g4,g7)
    c: Horizontal(g7,g8)
    c: Horizontal(g8,g10)
    c: Horizontal(g2,g5)
    c: Horizontal(g5,g11)
    c: Horizontal(g6,g9)
    c: Horizontal(g1,g6)
    c: Vertical(g2,g1)
    c: Vertical(g9,g11)
    c: DistanceY(g0) = -270
    c: DistanceX(g0) = -115
    c: DistanceX(g0,g2) = 35
    c: DistanceY(g2,g0) = 35
    c: DistanceY(g0,g1) = 35
    c: DistanceX(g0,g3) = 70
    c: DistanceX(g4) = -35
    c: DistanceX(g7) = 35
    c: DistanceX(g8) = 45
    c: DistanceX(g8,g10) = 70
    c: DistanceX(g8,g11) = 35
FEATURE [Part::Extrusion] Extrude119  label="m3Cuts"
  Base = -> Sketch220
  Dir = (0,0,1)
  DirMode = 2
  FaceMakerClass = Part::FaceMakerBullseye
  FaceMakerMode = 3
  LengthFwd = 60
  LengthRev = 0
  Solid = true
  Symmetric = false
FEATURE [Sketcher::SketchObject] Sketch224
  ArcFitTolerance = 0
  FullyConstrained = true
  MakeInternals = false
  Placement = pos=(24,0,0) rot=(0.57735,0.57735,0.57735;2.0944rad)
  sketch-geometry (2):
    g0: Circle CenterX=-277.6 CenterY=19.15 CenterZ=0 NormalX=0 NormalY=0 NormalZ=1 AngleXU=0 Radius=1.6
    g1: Circle CenterX=-262.4 CenterY=19.15 CenterZ=0 NormalX=0 NormalY=0 NormalZ=1 AngleXU=0 Radius=1.6
  constraints (6):
    c: Horizontal(g1,g0)
    c: Equal(g1,g0)
    c: Diameter(g1) = 3.2
    c: DistanceX(g0) = -277.6
    c: DistanceY(g0) = 19.15
    c: DistanceX(g0,g1) = 15.2
FEATURE [Part::Extrusion] Extrude123
  Base = -> Sketch224
  Dir = (1,0,0)
  DirMode = 2
  FaceMakerClass = Part::FaceMakerBullseye
  FaceMakerMode = 3
  LengthFwd = 30
  LengthRev = 0
  Solid = true
  Symmetric = false
FEATURE [Sketcher::SketchObject] Sketch225
  ArcFitTolerance = 0
  FullyConstrained = true
  MakeInternals = false
  Placement = pos=(0,0,-22) rot=(0,0,1;0rad)
  sketch-geometry (14):
    g0: LineSegment StartX=-2e-16 StartY=-267 StartZ=0 EndX=9.52628 EndY=-261.5 EndZ=0
    g1: LineSegment StartX=9.52628 StartY=-261.5 StartZ=0 EndX=9.52628 EndY=-250.5 EndZ=0
    g2: LineSegment StartX=9.52628 StartY=-250.5 StartZ=0 EndX=2e-16 EndY=-245 EndZ=0
    g3: LineSegment StartX=0 StartY=-245 StartZ=0 EndX=-9.52628 EndY=-250.5 EndZ=0
    g4: LineSegment StartX=-9.52628 StartY=-250.5 StartZ=0 EndX=-9.52628 EndY=-261.5 EndZ=0
    g5: LineSegment StartX=-9.52628 StartY=-261.5 StartZ=0 EndX=-2e-16 EndY=-267 EndZ=0
    g6: Circle [constr] CenterX=0 CenterY=-256 CenterZ=0 NormalX=0 NormalY=0 NormalZ=1 AngleXU=0 Radius=11
    g7: LineSegment StartX=67 StartY=-267 StartZ=0 EndX=76.5263 EndY=-261.5 EndZ=0
    g8: LineSegment StartX=76.5263 StartY=-261.5 StartZ=0 EndX=76.5263 EndY=-250.5 EndZ=0
    g9: LineSegment StartX=76.5263 StartY=-250.5 StartZ=0 EndX=67 EndY=-245 EndZ=0
    g10: LineSegment StartX=67 StartY=-245 StartZ=0 EndX=57.4737 EndY=-250.5 EndZ=0
    g11: LineSegment StartX=57.4737 StartY=-250.5 StartZ=0 EndX=57.4737 EndY=-261.5 EndZ=0
    g12: LineSegment StartX=57.4737 StartY=-261.5 StartZ=0 EndX=67 EndY=-267 EndZ=0
    g13: Circle [constr] CenterX=67 CenterY=-256 CenterZ=0 NormalX=0 NormalY=0 NormalZ=1 AngleXU=0 Radius=11
  constraints (34):
    c: Coincident(g0,g1)
    c: Coincident(g1,g2)
    c: Coincident(g2,g3)
    c: Coincident(g3,g4)
    c: Coincident(g4,g5)
    c: Coincident(g5,g0)
    c: Equal(g0, g1-g5) x5
    c: PointOnObject(g0,g6)
    c: PointOnObject(g1,g6)
    c: PointOnObject(g2,g6)
    c: PointOnObject(g3,g6)
    c: PointOnObject(g4,g6)
    c: PointOnObject(g5,g6)
    c: Coincident(g7,g8)
    c: Coincident(g8,g9)
    c: Coincident(g9,g10)
    c: Coincident(g10,g11)
    c: Coincident(g11,g12)
    c: Coincident(g12,g7)
    c: Equal(g7, g8-g12) x5
    c: PointOnObject(g7,g13)
    c: PointOnObject(g8,g13)
    c: PointOnObject(g9,g13)
    c: PointOnObject(g10,g13)
    c: PointOnObject(g11,g13)
    c: PointOnObject(g12,g13)
    c: Horizontal(g6,g13)
    c: Vertical(g6,g2)
    c: DistanceX(g6) = 0
    c: DistanceY(g6) = -256
    c: Diameter(g6) = 22
    c: Vertical(g13,g7)
    c: Diameter(g13) = 22
    c: DistanceX(g13) = 67
FEATURE [Part::Extrusion] Extrude124
  Base = -> Sketch225
  Dir = (0,0,1)
  DirMode = 2
  FaceMakerClass = Part::FaceMakerBullseye
  FaceMakerMode = 3
  LengthFwd = 6
  LengthRev = 0
  Solid = true
  Symmetric = false
FEATURE [Part::MultiFuse] Fusion253  label="pg7Cuts"
  Shapes = -> [Extrude123,Extrude124]
FEATURE [Sketcher::SketchObject] Sketch226
  ArcFitTolerance = 0
  FullyConstrained = true
  MakeInternals = false
  Placement = pos=(0,-232,0) rot=(1,0,0;1.5708rad)
  sketch-geometry (8):
    g0: LineSegment StartX=-13 StartY=6 StartZ=0 EndX=13 EndY=6 EndZ=0
    g1: LineSegment StartX=13 StartY=6 StartZ=0 EndX=13 EndY=-20 EndZ=0
    g2: LineSegment StartX=13 StartY=-20 StartZ=0 EndX=-13 EndY=-20 EndZ=0
    g3: LineSegment StartX=-13 StartY=-20 StartZ=0 EndX=-13 EndY=6 EndZ=0
    g4: LineSegment StartX=-18 StartY=11 StartZ=0 EndX=18 EndY=11 EndZ=0
    g5: LineSegment StartX=18 StartY=11 StartZ=0 EndX=18 EndY=-25 EndZ=0
    g6: LineSegment StartX=18 StartY=-25 StartZ=0 EndX=-18 EndY=-25 EndZ=0
    g7: LineSegment StartX=-18 StartY=-25 StartZ=0 EndX=-18 EndY=11 EndZ=0
  constraints (24):
    c: Coincident(g0,g1)
    c: Coincident(g1,g2)
    c: Coincident(g2,g3)
    c: Coincident(g3,g0)
    c: Horizontal(g0)
    c: Horizontal(g2)
    c: Vertical(g1)
    c: Vertical(g3)
    c: Coincident(g4,g5)
    c: Coincident(g5,g6)
    c: Coincident(g6,g7)
    c: Coincident(g7,g4)
    c: Horizontal(g4)
    c: Horizontal(g6)
    c: Vertical(g5)
    c: Vertical(g7)
    c: DistanceY(g6) = -25
    c: DistanceX(g2,g1) = 26
    c: DistanceX(g6) = -18
    c: DistanceX(g6,g2) = 5
    c: DistanceX(g5) = 18
    c: DistanceY(g2,g0) = 26
    c: DistanceY(g6,g2) = 5
    c: DistanceY(g0,g4) = 5
FEATURE [Part::Extrusion] Extrude125
  Base = -> Sketch226
  Dir = (0,-1,2e-16)
  DirMode = 2
  FaceMakerClass = Part::FaceMakerBullseye
  FaceMakerMode = 3
  LengthFwd = 32
  LengthRev = 0
  Reversed = true
  Solid = true
  Symmetric = false
FEATURE [Sketcher::SketchObject] Sketch227
  ArcFitTolerance = 0
  FullyConstrained = true
  MakeInternals = false
  Placement = pos=(0,0,11) rot=(0,0,1;0rad)
  sketch-geometry (1):
    g0: Circle CenterX=0 CenterY=-215 CenterZ=0 NormalX=0 NormalY=0 NormalZ=1 AngleXU=0 Radius=3.125
  constraints (3):
    c: DistanceX(g0) = 0
    c: DistanceY(g0) = -215
    c: Diameter(g0) = 6.25
FEATURE [Part::Extrusion] Extrude127
  Base = -> Sketch227
  Dir = (0,0,1)
  DirMode = 2
  FaceMakerClass = Part::FaceMakerBullseye
  FaceMakerMode = 3
  LengthFwd = 36
  LengthRev = 0
  Reversed = true
  Solid = true
  Symmetric = false
FEATURE [Sketcher::SketchObject] Sketch228
  ArcFitTolerance = 0
  FullyConstrained = true
  MakeInternals = false
  Placement = pos=(-18,0,0) rot=(0.57735,0.57735,0.57735;2.0944rad)
  sketch-geometry (1):
    g0: Circle CenterX=-215 CenterY=-7 CenterZ=0 NormalX=0 NormalY=0 NormalZ=1 AngleXU=0 Radius=3.25
  constraints (3):
    c: DistanceX(g0) = -215
    c: DistanceY(g0) = -7
    c: Diameter(g0) = 6.5
FEATURE [Part::Extrusion] Extrude126
  Base = -> Sketch228
  Dir = (1,0,0)
  DirMode = 2
  FaceMakerClass = Part::FaceMakerBullseye
  FaceMakerMode = 3
  LengthFwd = 36
  LengthRev = 0
  Solid = true
  Symmetric = false
FEATURE [Part::MultiFuse] Fusion252
  Shapes = -> [Extrude127,Extrude126]
FEATURE [Part::Cut] Cut082  label="in003"
  Base = -> Extrude125
  Tool = -> Fusion252
FEATURE [Part::Fillet] Fillet005
  Base = -> Cut082
  EdgeLinks = -> Cut082 [?Edge1,?Edge4,?Edge6,?Edge22]
  Edges = 4 edges r=2: [Edge1,Edge4,Edge6,Edge22]
FEATURE [Part::Fillet] Fillet006  label="tSlotHolder"
  Base = -> Fillet005
  EdgeLinks = -> Fillet005 [Edge4,Edge18,Edge20,Edge21,Edge22,Edge23,Edge24,Edge25,Edge26,Edge27,Edge28,Edge29]
  Edges = 12 edges r=2: [Edge4,Edge18,Edge20,Edge21,Edge22,Edge23,Edge24,Edge25,Edge26,Edge27,Edge28,Edge29]
FEATURE [Sketcher::SketchObject] Sketch229
  ArcFitTolerance = 0
  FullyConstrained = true
  MakeInternals = false
  Placement = pos=(0,0,-25) rot=(0,0,1;0rad)
  sketch-geometry (2):
    g0: Circle CenterX=0 CenterY=-256 CenterZ=0 NormalX=0 NormalY=0 NormalZ=1 AngleXU=0 Radius=6
    g1: Circle CenterX=67 CenterY=-256 CenterZ=0 NormalX=0 NormalY=0 NormalZ=1 AngleXU=0 Radius=6
  constraints (6):
    c: DistanceY(g0) = -256
    c: Horizontal(g0,g1)
    c: DistanceX(g0,g1) = 67
    c: DistanceX(g0) = 0
    c: Equal(g0,g1)
    c: Diameter(g0) = 12
FEATURE [Part::Extrusion] Extrude128  label="outCut"
  Base = -> Sketch229
  Dir = (0,0,1)
  DirMode = 2
  FaceMakerClass = Part::FaceMakerBullseye
  FaceMakerMode = 3
  LengthFwd = 5
  LengthRev = 0
  Solid = true
  Symmetric = false
FEATURE [Sketcher::SketchObject] Sketch233
  ArcFitTolerance = 0
  FullyConstrained = true
  MakeInternals = false
  Placement = pos=(0,0,-25) rot=(0,0,1;0rad)
  sketch-geometry (8):
    g0: ArcOfCircle CenterX=-80 CenterY=-270 CenterZ=0 NormalX=0 NormalY=0 NormalZ=1 AngleXU=0 Radius=40 StartAngle=1.5708 EndAngle=4.71239
    g1: ArcOfCircle CenterX=80 CenterY=-270 CenterZ=0 NormalX=0 NormalY=0 NormalZ=1 AngleXU=0 Radius=40 StartAngle=4.71239 EndAngle=7.85398
    g2: LineSegment StartX=-80 StartY=-310 StartZ=0 EndX=80 EndY=-310 EndZ=0
    g3: LineSegment StartX=80 StartY=-230 StartZ=0 EndX=-80 EndY=-230 EndZ=0
    g4: ArcOfCircle CenterX=-80 CenterY=-270 CenterZ=0 NormalX=0 NormalY=0 NormalZ=1 AngleXU=0 Radius=30 StartAngle=1.5708 EndAngle=4.71239
    g5: ArcOfCircle CenterX=80 CenterY=-270 CenterZ=0 NormalX=0 NormalY=0 NormalZ=1 AngleXU=0 Radius=30 StartAngle=4.71239 EndAngle=7.85398
    g6: LineSegment StartX=-80 StartY=-300 StartZ=0 EndX=80 EndY=-300 EndZ=0
    g7: LineSegment StartX=80 StartY=-240 StartZ=0 EndX=-80 EndY=-240 EndZ=0
  constraints (18):
    c: Tangent(g0,g2) = -1.5708
    c: Tangent(g2,g1) = -1.5708
    c: Tangent(g1,g3) = -1.5708
    c: Tangent(g3,g0) = -1.5708
    c: Equal(g0,g1)
    c: Horizontal(g2)
    c: DistanceY(g0) = -270
    c: DistanceX(g0) = -80
    c: DistanceX(g1) = 80
    c: Diameter(g0) = 80
    c: Tangent(g4,g6) = -1.5708
    c: Tangent(g6,g5) = -1.5708
    c: Tangent(g5,g7) = -1.5708
    c: Tangent(g7,g4) = -1.5708
    c: Equal(g4,g5)
    c: Coincident(g4,g0)
    c: Coincident(g5,g1)
    c: Diameter(g4) = 60
FEATURE [Part::Extrusion] Extrude133  label="outerBorder001"
  Base = -> Sketch233
  Dir = (0,0,1)
  DirMode = 2
  FaceMakerClass = Part::FaceMakerBullseye
  FaceMakerMode = 3
  LengthFwd = 53
  LengthRev = 0
  Solid = true
  Symmetric = false
FEATURE [Part::Fillet] Fillet013  label="outerHold001"
  Base = -> Extrude133
  EdgeLinks = -> Extrude133 [Edge9]
  Edges = 1 edges r=4: [Edge9]
FEATURE [Sketcher::SketchObject] Sketch234
  ArcFitTolerance = 0
  FullyConstrained = true
  MakeInternals = false
  Placement = pos=(0,0,-25) rot=(0,0,1;0rad)
  sketch-geometry (8):
    g0: ArcOfCircle CenterX=-80 CenterY=-270 CenterZ=0 NormalX=0 NormalY=0 NormalZ=1 AngleXU=0 Radius=30 StartAngle=5.55346 EndAngle=7.01291
    g1: LineSegment StartX=-57.6393 StartY=-250 StartZ=0 EndX=-22.3607 EndY=-250 EndZ=0
    g2: LineSegment StartX=-57.6393 StartY=-290 StartZ=0 EndX=-22.3607 EndY=-290 EndZ=0
    g3: ArcOfCircle CenterX=0 CenterY=-270 CenterZ=0 NormalX=0 NormalY=0 NormalZ=1 AngleXU=0 Radius=30 StartAngle=2.41186 EndAngle=3.87132
    g4: ArcOfCircle CenterX=0 CenterY=-270 CenterZ=0 NormalX=0 NormalY=0 NormalZ=1 AngleXU=0 Radius=30 StartAngle=5.55346 EndAngle=7.01291
    g5: ArcOfCircle CenterX=80 CenterY=-270 CenterZ=0 NormalX=0 NormalY=0 NormalZ=1 AngleXU=0 Radius=30 StartAngle=2.41186 EndAngle=3.87132
    g6: LineSegment StartX=22.3607 StartY=-250 StartZ=0 EndX=57.6393 EndY=-250 EndZ=0
    g7: LineSegment StartX=57.6393 StartY=-290 StartZ=0 EndX=22.3607 EndY=-290 EndZ=0
  constraints (27):
    c: Coincident(g1,g0)
    c: Horizontal(g1)
    c: Coincident(g2,g0)
    c: Horizontal(g2)
    c: PointOnObject(g3,g-2)
    c: Coincident(g3,g2)
    c: Coincident(g3,g1)
    c: Coincident(g4,g3)
    c: Coincident(g6,g4)
    c: Coincident(g6,g5)
    c: Horizontal(g6)
    c: Coincident(g7,g5)
    c: Coincident(g7,g4)
    c: Horizontal(g7)
    c: Horizontal(g0,g4)
    c: Horizontal(g2,g4)
    c: Equal(g3,g0)
    c: Equal(g3,g5)
    c: Equal(g3,g4)
    c: Diameter(g3) = 60
    c: DistanceY(g3) = -270
    c: Vertical(g0,g0)
    c: Vertical(g2,g1)
    c: Vertical(g5,g5)
    c: DistanceX(g5) = 80
    c: DistanceX(g0) = -80
    c: DistanceY(g4) = -250
FEATURE [Part::Extrusion] Extrude134  label="3WayHolds001"
  Base = -> Sketch234
  Dir = (0,0,1)
  DirMode = 2
  FaceMakerClass = Part::FaceMakerBullseye
  FaceMakerMode = 3
  LengthFwd = 53
  LengthRev = 0
  Solid = true
  Symmetric = false
FEATURE [Sketcher::SketchObject] Sketch235
  ArcFitTolerance = 0
  FullyConstrained = true
  MakeInternals = false
  Placement = pos=(0,0,-20) rot=(0,0,1;0rad)
  sketch-geometry (18):
    g0: ArcOfCircle CenterX=-80 CenterY=-240 CenterZ=0 NormalX=0 NormalY=0 NormalZ=1 AngleXU=0 Radius=20 StartAngle=3.48143 EndAngle=5.94335
    g1: ArcOfCircle CenterX=-80 CenterY=-300 CenterZ=0 NormalX=0 NormalY=0 NormalZ=1 AngleXU=0 Radius=20 StartAngle=0.339837 EndAngle=2.80176
    g2: ArcOfCircle CenterX=-80 CenterY=-270 CenterZ=0 NormalX=0 NormalY=0 NormalZ=1 AngleXU=0 Radius=30 StartAngle=0.891123 EndAngle=2.25047
    g3: ArcOfCircle CenterX=-80 CenterY=-270 CenterZ=0 NormalX=0 NormalY=0 NormalZ=1 AngleXU=0 Radius=30 StartAngle=4.03272 EndAngle=5.39206
    g4: LineSegment StartX=65 StartY=-286 StartZ=0 EndX=95 EndY=-286 EndZ=0
    g5: LineSegment StartX=95 StartY=-286 StartZ=0 EndX=95 EndY=-254 EndZ=0
    g6: LineSegment StartX=95 StartY=-254 StartZ=0 EndX=77 EndY=-254 EndZ=0
    g7: LineSegment StartX=77 StartY=-254 StartZ=0 EndX=77 EndY=-274 EndZ=0
    g8: LineSegment StartX=77 StartY=-274 StartZ=0 EndX=65 EndY=-274 EndZ=0
    g9: LineSegment StartX=65 StartY=-274 StartZ=0 EndX=65 EndY=-286 EndZ=0
    g10: Circle CenterX=-90 CenterY=-252.5 CenterZ=0 NormalX=0 NormalY=0 NormalZ=1 AngleXU=0 Radius=2
    g11: Circle CenterX=-70 CenterY=-252.5 CenterZ=0 NormalX=0 NormalY=0 NormalZ=1 AngleXU=0 Radius=2
    g12: Circle CenterX=-90 CenterY=-287.5 CenterZ=0 NormalX=0 NormalY=0 NormalZ=1 AngleXU=0 Radius=2
    g13: Circle CenterX=-70 CenterY=-287.5 CenterZ=0 NormalX=0 NormalY=0 NormalZ=1 AngleXU=0 Radius=2
    g14: Circle CenterX=69.84 CenterY=-280.6 CenterZ=0 NormalX=0 NormalY=0 NormalZ=1 AngleXU=0 Radius=1.6
    g15: Circle CenterX=90.16 CenterY=-280.6 CenterZ=0 NormalX=0 NormalY=0 NormalZ=1 AngleXU=0 Radius=1.6
    g16: Circle CenterX=90.16 CenterY=-267.9 CenterZ=0 NormalX=0 NormalY=0 NormalZ=1 AngleXU=0 Radius=1.6
    g17: Circle CenterX=86.5 CenterY=-259.25 CenterZ=0 NormalX=0 NormalY=0 NormalZ=1 AngleXU=0 Radius=1.6
  constraints (57):
    c: Vertical(g0,g1)
    c: Coincident(g2,g0)
    c: Coincident(g3,g2)
    c: Coincident(g3,g1)
    c: Coincident(g0,g2)
    c: Coincident(g1,g3)
    c: DistanceX(g2) = -80
    c: DistanceY(g2) = -270
    c: Equal(g3,g2)
    c: Diameter(g3) = 60
    c: Equal(g0,g1)
    c: Diameter(g0) = 40
    c: Vertical(g0,g2)
    c: DistanceY(g0) = -240
    c: DistanceY(g1) = -300
    c: Horizontal(g4)
    c: Coincident(g5,g4)
    c: Vertical(g5)
    c: Coincident(g6,g5)
    c: Horizontal(g6)
    c: Coincident(g7,g6)
    c: Vertical(g7)
    c: Coincident(g8,g7)
    c: Horizontal(g8)
    c: Coincident(g9,g8)
    c: Coincident(g9,g4)
    c: Vertical(g9)
    c: DistanceY(g4) = -286
    c: DistanceX(g4) = 65
    c: DistanceY(g4,g8) = 12
    c: DistanceX(g4,g4) = 30
    c: DistanceX(g6,g6) = 18
    c: DistanceY(g5,g5) = 32
    c: Horizontal(g13,g12)
    c: Horizontal(g10,g11)
    c: Vertical(g12,g10)
    c: Vertical(g13,g11)
    c: DistanceX(g12,g2) = 10
    c: DistanceY(g12) = -287.5
    c: DistanceX(g12,g13) = 20
    c: DistanceY(g12,g10) = 35
    c: Equal(g10,g11)
    c: Equal(g10,g13)
    c: Equal(g10,g12)
    c: Diameter(g10) = 4
    c: Horizontal(g14,g15)
    c: Vertical(g15,g16)
    c: DistanceX(g14,g15) = 20.32
    c: DistanceY(g14) = -280.6
    c: DistanceY(g15,g16) = 12.7
    c: DistanceX(g17,g16) = 3.66
    c: DistanceY(g16,g17) = 8.65
    c: Equal(g15,g16)
    c: Equal(g15,g17)
    c: Equal(g15,g14)
    c: Diameter(g15) = 3.2
    c: DistanceX(g4,g14) = 4.84
FEATURE [Part::Extrusion] Extrude135  label="i2cHolds001"
  Base = -> Sketch235
  Dir = (0,0,1)
  DirMode = 2
  FaceMakerClass = Part::FaceMakerBullseye
  FaceMakerMode = 3
  LengthFwd = 48
  LengthRev = 0
  Solid = true
  Symmetric = false
FEATURE [Sketcher::SketchObject] Sketch236
  ArcFitTolerance = 0
  FullyConstrained = true
  MakeInternals = false
  Placement = pos=(0,0,-20) rot=(0,0,1;0rad)
  sketch-geometry (12):
    g0: ArcOfCircle CenterX=-20 CenterY=-290 CenterZ=0 NormalX=0 NormalY=0 NormalZ=1 AngleXU=0 Radius=10 StartAngle=5.49779 EndAngle=8.63938
    g1: ArcOfCircle CenterX=20 CenterY=-290 CenterZ=0 NormalX=0 NormalY=0 NormalZ=1 AngleXU=0 Radius=10 StartAngle=0.785398 EndAngle=3.92699
    g2: ArcOfCircle CenterX=20 CenterY=-250 CenterZ=0 NormalX=0 NormalY=0 NormalZ=1 AngleXU=0 Radius=10 StartAngle=2.35619 EndAngle=5.49779
    g3: ArcOfCircle CenterX=-20 CenterY=-250 CenterZ=0 NormalX=0 NormalY=0 NormalZ=1 AngleXU=0 Radius=10 StartAngle=3.92699 EndAngle=7.06858
    g4: ArcOfCircle CenterX=0 CenterY=-270 CenterZ=0 NormalX=0 NormalY=0 NormalZ=1 AngleXU=0 Radius=30 StartAngle=2.01636 EndAngle=2.69603
    g5: ArcOfCircle CenterX=0 CenterY=-270 CenterZ=0 NormalX=0 NormalY=0 NormalZ=1 AngleXU=0 Radius=30 StartAngle=0.445561 EndAngle=1.12524
    g6: ArcOfCircle CenterX=0 CenterY=-270 CenterZ=0 NormalX=0 NormalY=0 NormalZ=1 AngleXU=0 Radius=30 StartAngle=5.15795 EndAngle=5.83762
    g7: ArcOfCircle CenterX=0 CenterY=-270 CenterZ=0 NormalX=0 NormalY=0 NormalZ=1 AngleXU=0 Radius=30 StartAngle=3.58715 EndAngle=4.26683
    g8: Circle CenterX=-17 CenterY=-253 CenterZ=0 NormalX=0 NormalY=0 NormalZ=1 AngleXU=0 Radius=1.6
    g9: Circle CenterX=17 CenterY=-253 CenterZ=0 NormalX=0 NormalY=0 NormalZ=1 AngleXU=0 Radius=1.6
    g10: Circle CenterX=17 CenterY=-287 CenterZ=0 NormalX=0 NormalY=0 NormalZ=1 AngleXU=0 Radius=1.6
    g11: Circle CenterX=-17 CenterY=-287 CenterZ=0 NormalX=0 NormalY=0 NormalZ=1 AngleXU=0 Radius=1.6
  constraints (41):
    c: Vertical(g0,g3)
    c: Vertical(g1,g2)
    c: Horizontal(g2,g3)
    c: Horizontal(g1,g0)
    c: Equal(g2,g3)
    c: Equal(g2,g0)
    c: Equal(g2,g1)
    c: Diameter(g2) = 20
    c: Horizontal(g0,g1)
    c: Horizontal(g1,g0)
    c: Angle(g0) = 3.14159
    c: Vertical(g0,g3)
    c: Vertical(g0,g3)
    c: Angle(g2) = 3.14159
    c: DistanceY(g0) = -290
    c: Coincident(g4,g3)
    c: Coincident(g4,g3)
    c: Coincident(g5,g4)
    c: Coincident(g5,g2)
    c: Coincident(g5,g2)
    c: Coincident(g6,g4)
    c: Coincident(g6,g1)
    c: Coincident(g6,g1)
    c: Coincident(g7,g4)
    c: Coincident(g7,g0)
    c: Coincident(g7,g0)
    c: DistanceX(g4) = 0
    c: DistanceY(g4) = -270
    c: DistanceX(g0,g4) = 20
    c: DistanceX(g11,g4) = 17
    c: DistanceY(g11,g4) = 17
    c: DistanceX(g4,g10) = 17
    c: DistanceY(g10,g4) = 17
    c: DistanceX(g4,g9) = 17
    c: Vertical(g8,g11)
    c: Horizontal(g8,g9)
    c: DistanceY(g4,g8) = 17
    c: Equal(g10,g9)
    c: Equal(g10,g8)
    c: Equal(g10,g11)
    c: Diameter(g10) = 3.2
FEATURE [Part::Extrusion] Extrude136  label="cameraHold001"
  Base = -> Sketch236
  Dir = (0,0,1)
  DirMode = 2
  FaceMakerClass = Part::FaceMakerBullseye
  FaceMakerMode = 3
  LengthFwd = 31
  LengthRev = 0
  Solid = true
  Symmetric = false
FEATURE [Sketcher::SketchObject] Sketch237
  ArcFitTolerance = 0
  FullyConstrained = true
  MakeInternals = false
  Placement = pos=(85,0,0) rot=(0.57735,0.57735,0.57735;2.0944rad)
  sketch-geometry (2):
    g0: ArcOfCircle CenterX=-270 CenterY=-20 CenterZ=0 NormalX=0 NormalY=0 NormalZ=1 AngleXU=0 Radius=15 StartAngle=0 EndAngle=3.14159
    g1: LineSegment StartX=-285 StartY=-20 StartZ=0 EndX=-255 EndY=-20 EndZ=0
  constraints (7):
    c: Horizontal(g0,g0)
    c: Horizontal(g0,g0)
    c: DistanceX(g0) = -270
    c: DistanceY(g0) = -20
    c: Diameter(g0) = 30
    c: Coincident(g1,g0)
    c: Coincident(g1,g0)
FEATURE [Part::Extrusion] Extrude137  label="WireCutcut003"
  Base = -> Sketch237
  Dir = (1,0,0)
  DirMode = 2
  FaceMakerClass = Part::FaceMakerBullseye
  FaceMakerMode = 3
  LengthFwd = 170
  LengthRev = 0
  Reversed = true
  Solid = true
  Symmetric = false
FEATURE [Sketcher::SketchObject] Sketch238
  ArcFitTolerance = 0
  FullyConstrained = true
  MakeInternals = false
  Placement = pos=(0,0,-25) rot=(0,0,1;0rad)
  sketch-geometry (3):
    g0: Circle CenterX=-80 CenterY=-270.2 CenterZ=0 NormalX=0 NormalY=0 NormalZ=1 AngleXU=0 Radius=40
    g1: Circle CenterX=0 CenterY=-270.2 CenterZ=0 NormalX=0 NormalY=0 NormalZ=1 AngleXU=0 Radius=40
    g2: Circle CenterX=80 CenterY=-270.2 CenterZ=0 NormalX=0 NormalY=0 NormalZ=1 AngleXU=0 Radius=40
  constraints (9):
    c: PointOnObject(g1,g-2)
    c: Diameter(g1) = 80
    c: Diameter(g0) = 80
    c: Horizontal(g1,g0)
    c: DistanceY(g0) = -270.2
    c: DistanceX(g0) = -80
    c: Horizontal(g2,g1)
    c: Diameter(g2) = 80
    c: DistanceX(g1,g2) = 80
FEATURE [Part::Extrusion] Extrude138  label="base006"
  Base = -> Sketch238
  Dir = (0,0,1)
  DirMode = 2
  FaceMakerClass = Part::FaceMakerBullseye
  FaceMakerMode = 3
  LengthFwd = 5
  LengthRev = 0
  Solid = true
  Symmetric = false
FEATURE [Part::Fillet] Fillet014  label="base007"
  Base = -> Extrude138
  EdgeLinks = -> Extrude138 [Edge2,Edge5,Edge8]
  Edges = 3 edges r=4: [Edge2,Edge5,Edge8]
FEATURE [Sketcher::SketchObject] Sketch239
  ArcFitTolerance = 0
  FullyConstrained = true
  MakeInternals = false
  Placement = pos=(0,0,-20) rot=(0,0,1;0rad)
  sketch-geometry (2):
    g0: Circle CenterX=0 CenterY=-270 CenterZ=0 NormalX=0 NormalY=0 NormalZ=1 AngleXU=0 Radius=30
    g1: Circle CenterX=0 CenterY=-270 CenterZ=0 NormalX=0 NormalY=0 NormalZ=1 AngleXU=0 Radius=40
  constraints (5):
    c: PointOnObject(g0,g-2)
    c: Coincident(g1,g0)
    c: DistanceY(g0) = -270
    c: Diameter(g0) = 60
    c: Diameter(g1) = 80
FEATURE [Part::Extrusion] Extrude139  label="domeHolds004"
  Base = -> Sketch239
  Dir = (0,0,1)
  DirMode = 2
  FaceMakerClass = Part::FaceMakerBullseye
  FaceMakerMode = 3
  LengthFwd = 48
  LengthRev = 0
  Solid = true
  Symmetric = false
FEATURE [Sketcher::SketchObject] Sketch240
  ArcFitTolerance = 0
  FullyConstrained = true
  MakeInternals = false
  Placement = pos=(0,0,-20) rot=(0,0,1;0rad)
  sketch-geometry (2):
    g0: Circle CenterX=0 CenterY=-270 CenterZ=0 NormalX=0 NormalY=0 NormalZ=1 AngleXU=0 Radius=30
    g1: Circle CenterX=0 CenterY=-270 CenterZ=0 NormalX=0 NormalY=0 NormalZ=1 AngleXU=0 Radius=40
  constraints (5):
    c: PointOnObject(g0,g-2)
    c: Coincident(g1,g0)
    c: DistanceY(g0) = -270
    c: Diameter(g0) = 60
    c: Diameter(g1) = 80
FEATURE [Part::Extrusion] Extrude140  label="domeHolds005"
  Base = -> Sketch240
  Dir = (0,0,1)
  DirMode = 2
  FaceMakerClass = Part::FaceMakerBullseye
  FaceMakerMode = 3
  LengthFwd = 48
  LengthRev = 0
  Placement = pos=(80,0,0) rot=(0,0,1;0rad)
  Solid = true
  Symmetric = false
FEATURE [Sketcher::SketchObject] Sketch241
  ArcFitTolerance = 0
  FullyConstrained = true
  MakeInternals = false
  Placement = pos=(0,0,-20) rot=(0,0,1;0rad)
  sketch-geometry (2):
    g0: Circle CenterX=0 CenterY=-270 CenterZ=0 NormalX=0 NormalY=0 NormalZ=1 AngleXU=0 Radius=30
    g1: Circle CenterX=0 CenterY=-270 CenterZ=0 NormalX=0 NormalY=0 NormalZ=1 AngleXU=0 Radius=40
  constraints (5):
    c: PointOnObject(g0,g-2)
    c: Coincident(g1,g0)
    c: DistanceY(g0) = -270
    c: Diameter(g0) = 60
    c: Diameter(g1) = 80
FEATURE [Part::Extrusion] Extrude141  label="domeHolds006"
  Base = -> Sketch241
  Dir = (0,0,1)
  DirMode = 2
  FaceMakerClass = Part::FaceMakerBullseye
  FaceMakerMode = 3
  LengthFwd = 48
  LengthRev = 0
  Placement = pos=(-80,0,0) rot=(0,0,1;0rad)
  Solid = true
  Symmetric = false
FEATURE [Part::MultiFuse] Fusion257  label="domeHolds007"
  Shapes = -> [Extrude139,Extrude140,Extrude141]
FEATURE [Part::MultiFuse] Fusion258  label="mainLightModule007"
  Shapes = -> [Fillet014,Fillet013,Fusion257,Extrude134]
FEATURE [Part::Fillet] Fillet015  label="mainLightModule006"
  Base = -> Fusion258
  EdgeLinks = -> Fusion258 [Edge124,Edge127,Edge206,Edge218,Edge219,Edge220,Edge265,Edge268,Edge277,Edge279,Edge280,Edge281,Edge295,Edge297,Edge301,Edge302,Edge303]
  Edges = 17 edges r=4: [Edge124,Edge127,Edge206,Edge218,Edge219,Edge220,Edge265,Edge268,Edge277,Edge279,Edge280,Edge281,Edge295,Edge297,Edge301,Edge302,Edge303]
FEATURE [Part::Cut] Cut084  label="mainLightModule005"
  Base = -> Fillet015
  Tool = -> Extrude137
FEATURE [Part::MultiFuse] Fusion259  label="mainLightModule008"
  Shapes = -> [Cut084,Extrude135,Extrude136]
FEATURE [Part::MultiFuse] Fusion260  label="mainCuts"
  Shapes = -> [Fusion253,Fusion251,Extrude128,Extrude119]
FEATURE [Part::Cut] Cut085  label="mainLightModule"
  Base = -> Fusion259
  Tool = -> Fusion260
FEATURE [Part::MultiFuse] Fusion261  label="mainLightModule009"
  Shapes = -> [Extrude129,Cut085,Fillet006]
FEATURE [Part::Fillet] Fillet016
  Base = -> Fusion261
  EdgeLinks = -> Fusion261 [Edge277,Edge279,Edge489,Edge491]
  Edges = 4 edges r=4: [Edge277,Edge279,Edge489,Edge491]
FEATURE [Part::Fillet] Fillet017  label="mainLightModule010"
  Base = -> Fillet016
  EdgeLinks = -> Fillet016 [Edge555,Edge744,Edge745,Edge897,Edge898,Edge1054]
  Edges = 6 edges r=1: [Edge555,Edge744,Edge745,Edge897,Edge898,Edge1054]
FEATURE [Part::Compound] Compound  label="setItems"
  Links = -> [Part__Feature330,Cut018,Adafruit_AS7341_STEMMA_QT_v2,Clone,Compound001,Extrude097,Adafruit_INA219_STEMMA_QT_v7,PG7_Gland1,PG7_Gland002]
FEATURE [Part::Compound] Compound002  label="lightModule"
  Links = -> [Fillet017,Compound]
